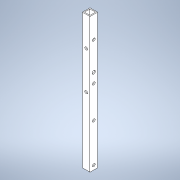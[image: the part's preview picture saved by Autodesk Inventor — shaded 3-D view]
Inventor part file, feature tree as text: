
AUTODESK INVENTOR PART (.ipt)
format: ipt  version: 2020.3 (Build 243373000, 373)  size: 144,896 bytes
history: native  units: mm
features: sketch x5, hole x4, other x1, extrude x1
ambient origin geometry x8: Origin, YZ Plane, XZ Plane, XY Plane, X Axis, Y Axis, Z Axis, Center Point
bodies: Body1 (feature_tree)
feature tree (11):
  other  "ソリッド1"
  extrude  "押し出し1"  Depth=9.0mm
  hole  "穴1"  [1 undecoded]
  hole  "穴2"  [1 undecoded]
  hole  "穴3"  [1 undecoded]
  hole  "穴4"  [1 undecoded]
  sketch  "スケッチ1"
  sketch  "スケッチ2"
  sketch  "スケッチ3"
  sketch  "スケッチ4"
  sketch  "スケッチ5"
note: 4 required parameter values undecoded (feature->parameter linkage not recoverable at this tier; creation-order binding heuristic only, values carry confidence <= 0.55)
